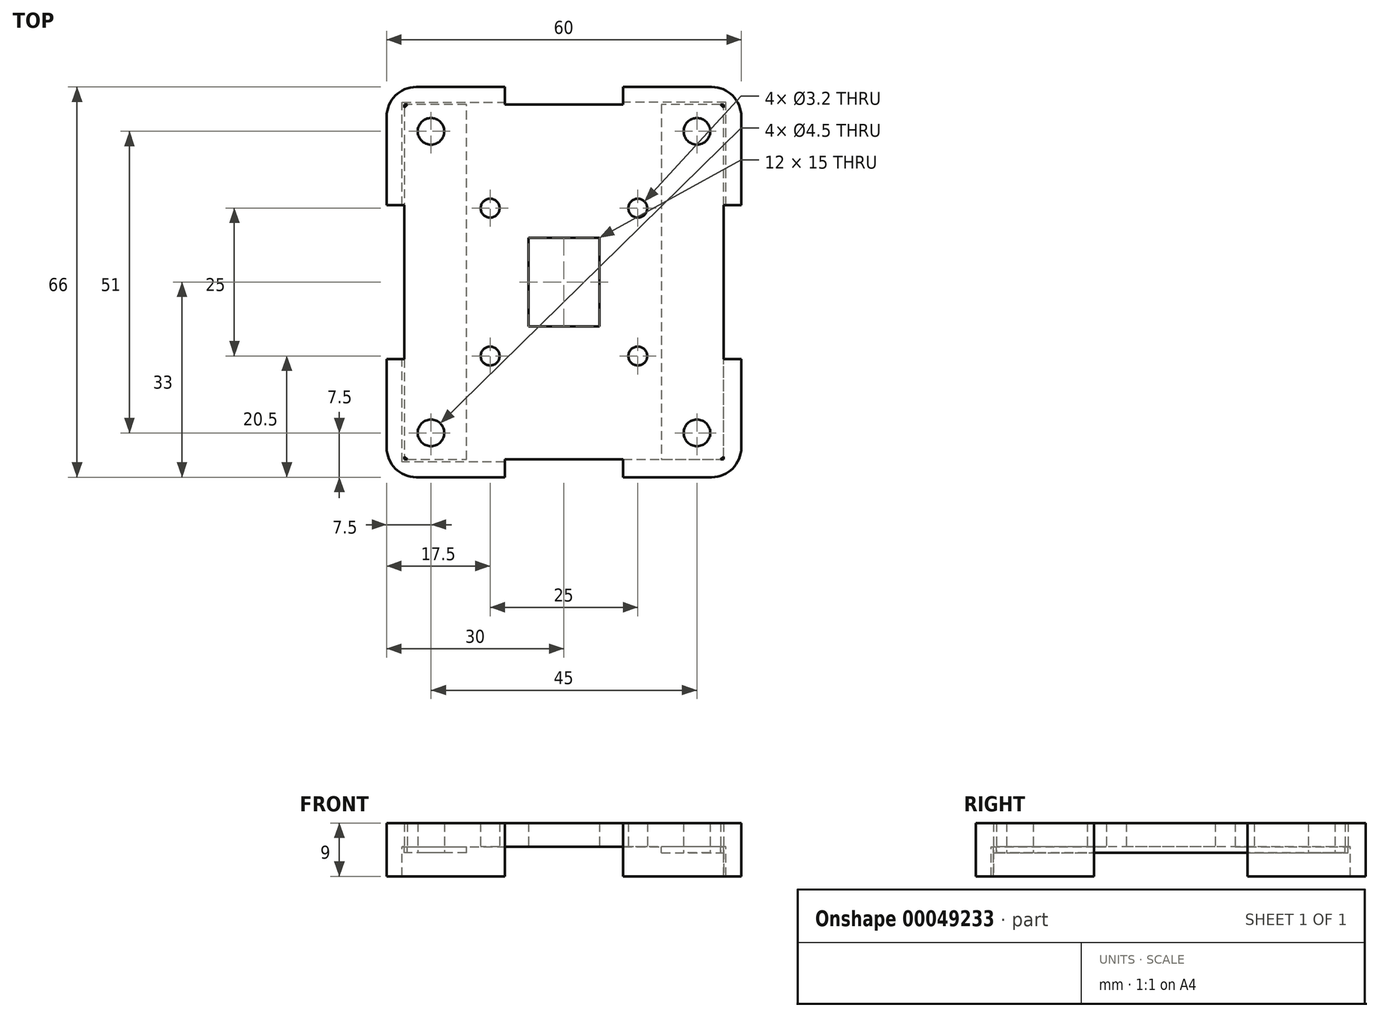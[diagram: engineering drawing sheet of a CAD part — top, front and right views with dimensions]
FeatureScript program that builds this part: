
annotation { "Feature Type Name" : "Feature", "Feature Type Description" : "" }
export const myFeature = defineFeature(function(context is Context, id is Id, definition is map)
    precondition{}
    {
        {
            var Q0;
            Q0=qCreatedBy(makeId("Top.planeOp"),FACE);
            var sketch = newSketch(context, id + "F0", { "sketchPlane" : qUnion([Q0])});
            skLineSegment(sketch, "E0", {"start": v(-26.5, -30) * mm, "end": v(-27, -29.5) * mm});
            skLineSegment(sketch, "E1", {"start": v(27, 29.5) * mm, "end": v(26.5, 30) * mm});
            skLineSegment(sketch, "E2", {"start": v(-27, -30) * mm, "end": v(26.5, -30) * mm});
            skLineSegment(sketch, "E3", {"start": v(26.6, -30) * mm, "end": v(27, -30) * mm});
            skLineSegment(sketch, "E4", {"start": v(26.5, -30) * mm, "end": v(26.6, -30) * mm});
            skLineSegment(sketch, "E5", {"start": v(-27, 30) * mm, "end": v(26.5, 30) * mm});
            skLineSegment(sketch, "E6", {"start": v(26.5, 30) * mm, "end": v(26.6, 30) * mm});
            skLineSegment(sketch, "E7", {"start": v(26.6, 30) * mm, "end": v(27, 30) * mm});
            skLineSegment(sketch, "E8", {"start": v(26.5, -30) * mm, "end": v(27, -29.5) * mm});
            skLineSegment(sketch, "E9", {"start": v(-27, 29.5) * mm, "end": v(-26.5, 30) * mm});
            skLineSegment(sketch, "E10", {"start": v(-27, -30) * mm, "end": v(-27, 29.5) * mm});
            skLineSegment(sketch, "E11", {"start": v(-27, 29.5) * mm, "end": v(-27, 30) * mm});
            skLineSegment(sketch, "E12", {"start": v(-26.6, -30) * mm, "end": v(-26.6, -29.9) * mm});
            skLineSegment(sketch, "E13", {"start": v(-26.6, 29.9) * mm, "end": v(-26.6, 30) * mm});
            skLineSegment(sketch, "E14", {"start": v(26.6, -30) * mm, "end": v(26.6, -29.9) * mm});
            skLineSegment(sketch, "E15", {"start": v(26.6, 29.9) * mm, "end": v(26.6, 30) * mm});
            skLineSegment(sketch, "E16", {"start": v(27, -30) * mm, "end": v(27, 29.5) * mm});
            skLineSegment(sketch, "E17", {"start": v(27, 29.5) * mm, "end": v(27, 30) * mm});
            skCircle(sketch, "E18", {"center": v(-22.5, -25.5) * mm, "radius": 1.6 * mm});
            skCircle(sketch, "E19", {"center": v(-22.5, -25.5) * mm, "radius": 2 * mm});
            skCircle(sketch, "E20", {"center": v(-22.5, -25.5) * mm, "radius": 2.25 * mm});
            skCircle(sketch, "E21", {"center": v(-22.5, 25.5) * mm, "radius": 1.6 * mm});
            skCircle(sketch, "E22", {"center": v(-22.5, 25.5) * mm, "radius": 2.25 * mm});
            skCircle(sketch, "E23", {"center": v(22.5, -25.5) * mm, "radius": 1.6 * mm});
            skCircle(sketch, "E24", {"center": v(22.5, -25.5) * mm, "radius": 2 * mm});
            skCircle(sketch, "E25", {"center": v(22.5, -25.5) * mm, "radius": 2.25 * mm});
            skCircle(sketch, "E26", {"center": v(22.5, 25.5) * mm, "radius": 1.6 * mm});
            skCircle(sketch, "E27", {"center": v(22.5, 25.5) * mm, "radius": 2 * mm});
            skCircle(sketch, "E28", {"center": v(22.5, 25.5) * mm, "radius": 2.25 * mm});
            skLineSegment(sketch, "E29", {"start": v(-24.75, -25.5) * mm, "end": v(-20.25, -25.5) * mm});
            skLineSegment(sketch, "E30", {"start": v(-22.5, -23.25) * mm, "end": v(-22.5, -27.75) * mm});
            skLineSegment(sketch, "E31", {"start": v(-24.75, 25.5) * mm, "end": v(-20.25, 25.5) * mm});
            skLineSegment(sketch, "E32", {"start": v(-22.5, 27.75) * mm, "end": v(-22.5, 23.25) * mm});
            skLineSegment(sketch, "E33", {"start": v(20.25, -25.5) * mm, "end": v(24.75, -25.5) * mm});
            skLineSegment(sketch, "E34", {"start": v(22.5, -23.25) * mm, "end": v(22.5, -27.75) * mm});
            skLineSegment(sketch, "E35", {"start": v(20.25, 25.5) * mm, "end": v(24.75, 25.5) * mm});
            skLineSegment(sketch, "E36", {"start": v(22.5, 27.75) * mm, "end": v(22.5, 23.25) * mm});
            skLineSegment(sketch, "E37", {"start": v(-24.5, -25.5) * mm, "end": v(-20.5, -25.5) * mm});
            skLineSegment(sketch, "E38", {"start": v(-22.5, -23.5) * mm, "end": v(-22.5, -27.5) * mm});
            skLineSegment(sketch, "E39", {"start": v(-26, -25.5) * mm, "end": v(-19, -25.5) * mm});
            skLineSegment(sketch, "E40", {"start": v(-22.5, -22) * mm, "end": v(-22.5, -29) * mm});
            skLineSegment(sketch, "E41", {"start": v(-24.5, 25.5) * mm, "end": v(-20.5, 25.5) * mm});
            skLineSegment(sketch, "E42", {"start": v(-22.5, 27.5) * mm, "end": v(-22.5, 23.5) * mm});
            skLineSegment(sketch, "E43", {"start": v(-26, 25.5) * mm, "end": v(-19, 25.5) * mm});
            skLineSegment(sketch, "E44", {"start": v(-22.5, 29) * mm, "end": v(-22.5, 22) * mm});
            skLineSegment(sketch, "E45", {"start": v(24.5, -25.5) * mm, "end": v(20.5, -25.5) * mm});
            skLineSegment(sketch, "E46", {"start": v(22.5, -27.5) * mm, "end": v(22.5, -23.5) * mm});
            skLineSegment(sketch, "E47", {"start": v(26, -25.5) * mm, "end": v(19, -25.5) * mm});
            skLineSegment(sketch, "E48", {"start": v(22.5, -29) * mm, "end": v(22.5, -22) * mm});
            skLineSegment(sketch, "E49", {"start": v(24.5, 25.5) * mm, "end": v(20.5, 25.5) * mm});
            skLineSegment(sketch, "E50", {"start": v(22.5, 23.5) * mm, "end": v(22.5, 27.5) * mm});
            skLineSegment(sketch, "E51", {"start": v(26, 25.5) * mm, "end": v(19, 25.5) * mm});
            skLineSegment(sketch, "E52", {"start": v(22.5, 22) * mm, "end": v(22.5, 29) * mm});
            skCircle(sketch, "E53.cCircle", {"center": v(-12.5, 12.5) * mm, "radius": 1.6 * mm});
            skPoint(sketch, "E53.0.midPoint", {"position": v(-11.13, 11.67) * mm});
            skCircle(sketch, "E54.cCircle", {"center": v(12.5, 12.5) * mm, "radius": 1.6 * mm});
            skCircle(sketch, "E55.cCircle", {"center": v(-12.5, -12.5) * mm, "radius": 1.6 * mm});
            skCircle(sketch, "E56.cCircle", {"center": v(12.5, -12.5) * mm, "radius": 1.6 * mm});
            skLineSegment(sketch, "E57", {"start": v(12.5, -12.5) * mm, "end": v(-12.5, 12.5) * mm, "construction": true});
            skLineSegment(sketch, "E58", {"start": v(12.5, 12.5) * mm, "end": v(-12.5, -12.5) * mm, "construction": true});
            skLineSegment(sketch, "E59.bottom", {"start": v(6, 7.5) * mm, "end": v(-6, 7.5) * mm});
            skLineSegment(sketch, "E59.top", {"start": v(6, -7.5) * mm, "end": v(-6, -7.5) * mm});
            skLineSegment(sketch, "E59.left", {"start": v(6, 7.5) * mm, "end": v(6, -7.5) * mm});
            skLineSegment(sketch, "E59.right", {"start": v(-6, 7.5) * mm, "end": v(-6, -7.5) * mm});
            skLineSegment(sketch, "E60", {"start": v(6, 0) * mm, "end": v(27, 0) * mm, "construction": true});
            skLineSegment(sketch, "E61", {"start": v(-6, 0) * mm, "end": v(-27, 0) * mm, "construction": true});
            skLineSegment(sketch, "E62", {"start": v(10, 30) * mm, "end": v(10, 33) * mm});
            skLineSegment(sketch, "E63", {"start": v(10, 33) * mm, "end": v(30, 33) * mm});
            skLineSegment(sketch, "E64", {"start": v(30, 33) * mm, "end": v(30, 13) * mm});
            skLineSegment(sketch, "E65", {"start": v(30, 13) * mm, "end": v(27, 13) * mm});
            skLineSegment(sketch, "E66", {"start": v(-27, -13) * mm, "end": v(-30, -13) * mm});
            skLineSegment(sketch, "E67", {"start": v(-30, -13) * mm, "end": v(-30, -33) * mm});
            skLineSegment(sketch, "E68", {"start": v(-30, -33) * mm, "end": v(-10, -33) * mm});
            skLineSegment(sketch, "E69", {"start": v(-10, -33) * mm, "end": v(-10, -30) * mm});
            skLineSegment(sketch, "E70", {"start": v(10, -30) * mm, "end": v(10, -33) * mm});
            skLineSegment(sketch, "E71", {"start": v(10, -33) * mm, "end": v(30, -33) * mm});
            skLineSegment(sketch, "E72", {"start": v(30, -33) * mm, "end": v(30, -13) * mm});
            skLineSegment(sketch, "E73", {"start": v(30, -13) * mm, "end": v(27, -13) * mm});
            skLineSegment(sketch, "E74", {"start": v(-27, 13) * mm, "end": v(-30, 13) * mm});
            skLineSegment(sketch, "E75", {"start": v(-30, 13) * mm, "end": v(-30, 33) * mm});
            skLineSegment(sketch, "E76", {"start": v(-30, 33) * mm, "end": v(-10, 33) * mm});
            skLineSegment(sketch, "E77", {"start": v(-10, 33) * mm, "end": v(-10, 30) * mm});
            skLineSegment(sketch, "E78", {"start": v(0, -7.5) * mm, "end": v(0, -30) * mm, "construction": true});
            skLineSegment(sketch, "E79", {"start": v(0, 7.5) * mm, "end": v(0, 30) * mm, "construction": true});
            skSolve(sketch);
        }
        {
            var Q0;
            Q0=makeQuery(id+"F0.imprint","IMPRINT",FACE,{"disambiguationData":[TD([[makeQuery(id+"F0.imprint","IMPRINT",EDGE,{"derivedFrom":sQuery(id+"F0.wireOp",EDGE,"E53.cCircle")}),-1.0]])]});
            var Q1;
            {var subQ8=sQuery(id+"F0.wireOp",EDGE,"E66");Q1=makeQuery(id+"F0.imprint","IMPRINT",FACE,{"disambiguationData":[TD([[makeQuery(id+"F0.imprint","IMPRINT",EDGE,{"derivedFrom":subQ8}),1.0]])]});}
            var Q2;
            {var subQ1=sQuery(id+"F0.wireOp",EDGE,"E3");Q2=makeQuery(id+"F0.imprint","IMPRINT",FACE,{"disambiguationData":[TD([[makeQuery(id+"F0.imprint","IMPRINT",EDGE,{"derivedFrom":subQ1}),-1.0]])]});}
            var Q3;
            {var subQ4=sQuery(id+"F0.wireOp",EDGE,"E6");Q3=makeQuery(id+"F0.imprint","IMPRINT",FACE,{"disambiguationData":[TD([[makeQuery(id+"F0.imprint","IMPRINT",EDGE,{"derivedFrom":subQ4}),1.0]])]});}
            var Q4;
            {var subQ0=sQuery(id+"F0.wireOp",EDGE,"E11");Q4=makeQuery(id+"F0.imprint","IMPRINT",FACE,{"disambiguationData":[TD([[makeQuery(id+"F0.imprint","IMPRINT",EDGE,{"derivedFrom":subQ0}),1.0]])]});}
            extrude(context, id + "F1", {"entities" : qUnion([Q0, Q1, Q2, Q3, Q4]), "depth" : 4 * mm, "offsetDistance" : 25 * mm});
        }
        {
            var Q0;
            Q0=makeQuery(id+"F1.opExtrude","CAP_FACE",FACE,{"disambiguationData":[OSD([sQuery(id+"F0.wireOp",EDGE,"E0"),sQuery(id+"F0.wireOp",EDGE,"E1"),sQuery(id+"F0.wireOp",EDGE,"E2"),sQuery(id+"F0.wireOp",EDGE,"E5"),sQuery(id+"F0.wireOp",EDGE,"E8"),sQuery(id+"F0.wireOp",EDGE,"E9"),sQuery(id+"F0.wireOp",EDGE,"E10"),sQuery(id+"F0.wireOp",EDGE,"E16"),sQuery(id+"F0.wireOp",EDGE,"E20"),sQuery(id+"F0.wireOp",EDGE,"E22"),sQuery(id+"F0.wireOp",EDGE,"E25"),sQuery(id+"F0.wireOp",EDGE,"E28"),sQuery(id+"F0.wireOp",EDGE,"E53.cCircle"),sQuery(id+"F0.wireOp",EDGE,"E54.cCircle"),sQuery(id+"F0.wireOp",EDGE,"E55.cCircle"),sQuery(id+"F0.wireOp",EDGE,"E56.cCircle")])],"isStart":true});
            var sketch = newSketch(context, id + "F2", { "sketchPlane" : qUnion([Q0])});
            skLineSegment(sketch, "E80", {"start": v(-16.5, 30) * mm, "end": v(-16.5, -30) * mm});
            skLineSegment(sketch, "E81", {"start": v(-16.5, -30) * mm, "end": v(-26.5, -30) * mm});
            skLineSegment(sketch, "E82", {"start": v(-26.5, -30) * mm, "end": v(-27, -29.5) * mm});
            skLineSegment(sketch, "E83", {"start": v(-27, -29.5) * mm, "end": v(-27, 29.5) * mm});
            skLineSegment(sketch, "E84", {"start": v(-27, 29.5) * mm, "end": v(-26.5, 30) * mm});
            skLineSegment(sketch, "E85", {"start": v(-26.5, 30) * mm, "end": v(-16.5, 30) * mm});
            skLineSegment(sketch, "E86", {"start": v(16.5, -30) * mm, "end": v(16.5, 30) * mm});
            skLineSegment(sketch, "E87", {"start": v(16.5, 30) * mm, "end": v(26.5, 30) * mm});
            skLineSegment(sketch, "E88", {"start": v(26.5, 30) * mm, "end": v(27, 29.5) * mm});
            skLineSegment(sketch, "E89", {"start": v(27, 29.5) * mm, "end": v(27, -29.5) * mm});
            skLineSegment(sketch, "E90", {"start": v(27, -29.5) * mm, "end": v(26.5, -30) * mm});
            skLineSegment(sketch, "E91", {"start": v(26.5, -30) * mm, "end": v(16.5, -30) * mm});
            skCircle(sketch, "E92", {"center": v(-22.5, 25.5) * mm, "radius": 2.25 * mm});
            skCircle(sketch, "E93", {"center": v(-22.5, -25.5) * mm, "radius": 2.25 * mm});
            skCircle(sketch, "E94", {"center": v(22.5, -25.5) * mm, "radius": 2.25 * mm});
            skCircle(sketch, "E95", {"center": v(22.5, 25.5) * mm, "radius": 2.25 * mm});
            skLineSegment(sketch, "E96", {"start": v(-27.4, 13) * mm, "end": v(-30, 13) * mm});
            skLineSegment(sketch, "E97", {"start": v(-30, 13) * mm, "end": v(-30, 33) * mm});
            skLineSegment(sketch, "E98", {"start": v(-30, 33) * mm, "end": v(-10, 33) * mm});
            skLineSegment(sketch, "E99", {"start": v(-10, 33) * mm, "end": v(-10, 30.4) * mm});
            skLineSegment(sketch, "E100", {"start": v(-10, 30.4) * mm, "end": v(-27.4, 30.4) * mm});
            skLineSegment(sketch, "E101", {"start": v(-27.4, 30.4) * mm, "end": v(-27.4, 13) * mm});
            skLineSegment(sketch, "E102", {"start": v(10, 33) * mm, "end": v(30, 33) * mm});
            skLineSegment(sketch, "E103", {"start": v(30, 33) * mm, "end": v(30, 13) * mm});
            skLineSegment(sketch, "E104", {"start": v(30, 13) * mm, "end": v(27.4, 13) * mm});
            skLineSegment(sketch, "E105", {"start": v(27.4, 13) * mm, "end": v(27.4, 30.4) * mm});
            skLineSegment(sketch, "E106", {"start": v(27.4, 30.4) * mm, "end": v(10, 30.4) * mm});
            skLineSegment(sketch, "E107", {"start": v(10, 30.4) * mm, "end": v(10, 33) * mm});
            skLineSegment(sketch, "E108", {"start": v(27.4, -13) * mm, "end": v(27.4, -30.4) * mm});
            skLineSegment(sketch, "E109", {"start": v(27.4, -30.4) * mm, "end": v(10, -30.4) * mm});
            skLineSegment(sketch, "E110", {"start": v(10, -30.4) * mm, "end": v(10, -33) * mm});
            skLineSegment(sketch, "E111", {"start": v(10, -33) * mm, "end": v(30, -33) * mm});
            skLineSegment(sketch, "E112", {"start": v(30, -33) * mm, "end": v(30, -13) * mm});
            skLineSegment(sketch, "E113", {"start": v(30, -13) * mm, "end": v(27.4, -13) * mm});
            skLineSegment(sketch, "E114", {"start": v(-27.4, -13) * mm, "end": v(-27.4, -30.4) * mm});
            skLineSegment(sketch, "E115", {"start": v(-27.4, -30.4) * mm, "end": v(-10, -30.4) * mm});
            skLineSegment(sketch, "E116", {"start": v(-10, -30.4) * mm, "end": v(-10, -33) * mm});
            skLineSegment(sketch, "E117", {"start": v(-10, -33) * mm, "end": v(-30, -33) * mm});
            skLineSegment(sketch, "E118", {"start": v(-30, -33) * mm, "end": v(-30, -13) * mm});
            skLineSegment(sketch, "E119", {"start": v(-30, -13) * mm, "end": v(-27.4, -13) * mm});
            skSolve(sketch);
        }
        {
            var Q0;
            {var subQ3=sQuery(id+"F2.wireOp",EDGE,"E80");Q0=makeQuery(id+"F2.imprint","IMPRINT",FACE,{"disambiguationData":[TD([[makeQuery(id+"F2.imprint","IMPRINT",EDGE,{"derivedFrom":subQ3}),-1.0]])]});}
            var Q1;
            {var subQ3=sQuery(id+"F2.wireOp",EDGE,"E86");Q1=makeQuery(id+"F2.imprint","IMPRINT",FACE,{"disambiguationData":[TD([[makeQuery(id+"F2.imprint","IMPRINT",EDGE,{"derivedFrom":subQ3}),-1.0]])]});}
            extrude(context, id + "F3", {"entities" : qUnion([Q0, Q1]), "operationType" : NewBodyOperationType.ADD, "depth" : 1 * mm, "offsetDistance" : 25 * mm});
        }
        {
            var Q0;
            Q0=makeQuery(id+"F2.imprint","IMPRINT",FACE,{"disambiguationData":[TD([[makeQuery(id+"F2.imprint","IMPRINT",EDGE,{"derivedFrom":sQuery(id+"F2.wireOp",EDGE,"E96")}),-1.0]])]});
            var Q1;
            Q1=makeQuery(id+"F2.imprint","IMPRINT",FACE,{"disambiguationData":[TD([[makeQuery(id+"F2.imprint","IMPRINT",EDGE,{"derivedFrom":sQuery(id+"F2.wireOp",EDGE,"E114")}),-1.0]])]});
            var Q2;
            Q2=makeQuery(id+"F2.imprint","IMPRINT",FACE,{"disambiguationData":[TD([[makeQuery(id+"F2.imprint","IMPRINT",EDGE,{"derivedFrom":sQuery(id+"F2.wireOp",EDGE,"E108")}),1.0]])]});
            var Q3;
            {var subQ1=sQuery(id+"F0.wireOp",EDGE,"E3");Q3=makeQuery(id+"F0.imprint","IMPRINT",FACE,{"disambiguationData":[TD([[makeQuery(id+"F0.imprint","IMPRINT",EDGE,{"derivedFrom":subQ1}),-1.0]])]});}
            extrude(context, id + "F4", {"entities" : qUnion([Q0, Q1, Q2, Q3]), "operationType" : NewBodyOperationType.ADD, "depth" : 5 * mm, "offsetDistance" : 25 * mm});
        }
        {
            var Q0;
            {var subQ0=sQuery(id+"F0.wireOp",EDGE,"E72");var subQ1=sQuery(id+"F0.wireOp",EDGE,"E71");Q0=makeQuery(id+"F4.boolean.opBoolean","MERGE",EDGE,{"derivedFrom":[makeQuery(id+"F1.opExtrude","SWEPT_EDGE",EDGE,{"disambiguationData":[OSD([subQ1,subQ0])]}),makeQuery(id+"F4.opExtrude","SWEPT_EDGE",EDGE,{"disambiguationData":[OSD([subQ1,subQ0])]})]});}
            var Q1;
            Q1=makeQuery(id+"F4.boolean.opBoolean","MERGE",EDGE,{"derivedFrom":[makeQuery(id+"F1.opExtrude","SWEPT_EDGE",EDGE,{"disambiguationData":[OSD([sQuery(id+"F0.wireOp",EDGE,"E63"),sQuery(id+"F0.wireOp",EDGE,"E64")])]}),makeQuery(id+"F4.opExtrude","SWEPT_EDGE",EDGE,{"disambiguationData":[OSD([sQuery(id+"F2.wireOp",EDGE,"E111"),sQuery(id+"F2.wireOp",EDGE,"E112")])]})]});
            var Q2;
            Q2=makeQuery(id+"F4.boolean.opBoolean","MERGE",EDGE,{"derivedFrom":[makeQuery(id+"F1.opExtrude","SWEPT_EDGE",EDGE,{"disambiguationData":[OSD([sQuery(id+"F0.wireOp",EDGE,"E75"),sQuery(id+"F0.wireOp",EDGE,"E76")])]}),makeQuery(id+"F4.opExtrude","SWEPT_EDGE",EDGE,{"disambiguationData":[OSD([sQuery(id+"F2.wireOp",EDGE,"E117"),sQuery(id+"F2.wireOp",EDGE,"E118")])]})]});
            var Q3;
            Q3=makeQuery(id+"F4.boolean.opBoolean","MERGE",EDGE,{"derivedFrom":[makeQuery(id+"F1.opExtrude","SWEPT_EDGE",EDGE,{"disambiguationData":[OSD([sQuery(id+"F0.wireOp",EDGE,"E67"),sQuery(id+"F0.wireOp",EDGE,"E68")])]}),makeQuery(id+"F4.opExtrude","SWEPT_EDGE",EDGE,{"disambiguationData":[OSD([sQuery(id+"F2.wireOp",EDGE,"E97"),sQuery(id+"F2.wireOp",EDGE,"E98")])]})]});
            fillet(context, id + "F5", {"entities" : qUnion([Q0, Q1, Q2, Q3]), "radius" : 5 * mm, "tangentPropagation" : true, "allowEdgeOverflow" : false});
        }
    });
